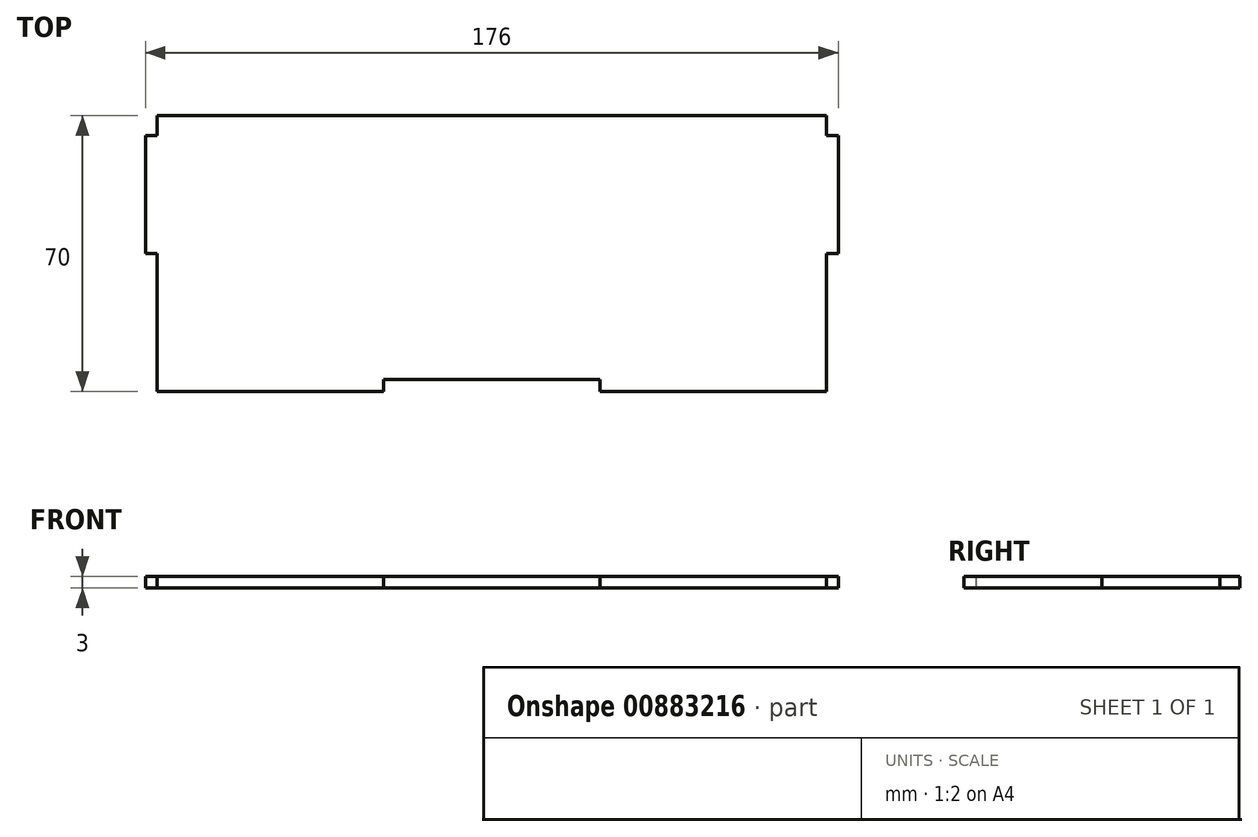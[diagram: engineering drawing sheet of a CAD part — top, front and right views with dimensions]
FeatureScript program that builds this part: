
annotation { "Feature Type Name" : "Feature", "Feature Type Description" : "" }
export const myFeature = defineFeature(function(context is Context, id is Id, definition is map)
    precondition{}
    {
        {
            var Q0;
            Q0=qCreatedBy(makeId("Top.planeOp"),FACE);
            var sketch = newSketch(context, id + "F0", { "sketchPlane" : qUnion([Q0])});
            skLineSegment(sketch, "E0.bottom", {"start": v(85, 35) * mm, "end": v(-85, 35) * mm});
            skLineSegment(sketch, "E0.top", {"start": v(85, -35) * mm, "end": v(-85, -35) * mm});
            skLineSegment(sketch, "E0.left", {"start": v(85, 35) * mm, "end": v(85, -35) * mm});
            skLineSegment(sketch, "E0.right", {"start": v(-85, 35) * mm, "end": v(-85, -35) * mm});
            skPoint(sketch, "E0.middle", {"position": v(0, 0) * mm});
            skLineSegment(sketch, "E1", {"start": v(-85, 0) * mm, "end": v(-88, 0) * mm});
            skLineSegment(sketch, "E2", {"start": v(-88, 0) * mm, "end": v(-88, 30) * mm});
            skLineSegment(sketch, "E3", {"start": v(-88, 30) * mm, "end": v(-85, 30) * mm});
            skLineSegment(sketch, "E4.MirrorCS", {"start": v(85, 0) * mm, "end": v(88, 0) * mm});
            skLineSegment(sketch, "E5.MirrorCS", {"start": v(88, 0) * mm, "end": v(88, 30) * mm});
            skLineSegment(sketch, "E6.MirrorCS", {"start": v(88, 30) * mm, "end": v(85, 30) * mm});
            skLineSegment(sketch, "E7", {"start": v(-27.5, -35) * mm, "end": v(-27.5, -32) * mm});
            skLineSegment(sketch, "E8", {"start": v(-27.5, -32) * mm, "end": v(27.5, -32) * mm});
            skLineSegment(sketch, "E9", {"start": v(27.5, -32) * mm, "end": v(27.5, -35) * mm});
            skSolve(sketch);
        }
        {
            var Q0;
            {var subQ0=sQuery(id+"F0.wireOp",EDGE,"E4.MirrorCS");Q0=makeQuery(id+"F0.imprint","IMPRINT",FACE,{"disambiguationData":[TD([[makeQuery(id+"F0.imprint","IMPRINT",EDGE,{"derivedFrom":subQ0}),1.0]])]});}
            var Q1;
            {var subQ0=sQuery(id+"F0.wireOp",EDGE,"E1");Q1=makeQuery(id+"F0.imprint","IMPRINT",FACE,{"disambiguationData":[TD([[makeQuery(id+"F0.imprint","IMPRINT",EDGE,{"derivedFrom":subQ0}),-1.0]])]});}
            var Q2;
            {var subQ5=sQuery(id+"F0.wireOp",EDGE,"E0.bottom");Q2=makeQuery(id+"F0.imprint","IMPRINT",FACE,{"disambiguationData":[TD([[makeQuery(id+"F0.imprint","IMPRINT",EDGE,{"derivedFrom":subQ5}),1.0]])]});}
            extrude(context, id + "F1", {"entities" : qUnion([Q0, Q1, Q2]), "depth" : 3 * mm, "offsetDistance" : 25 * mm});
        }
    });
